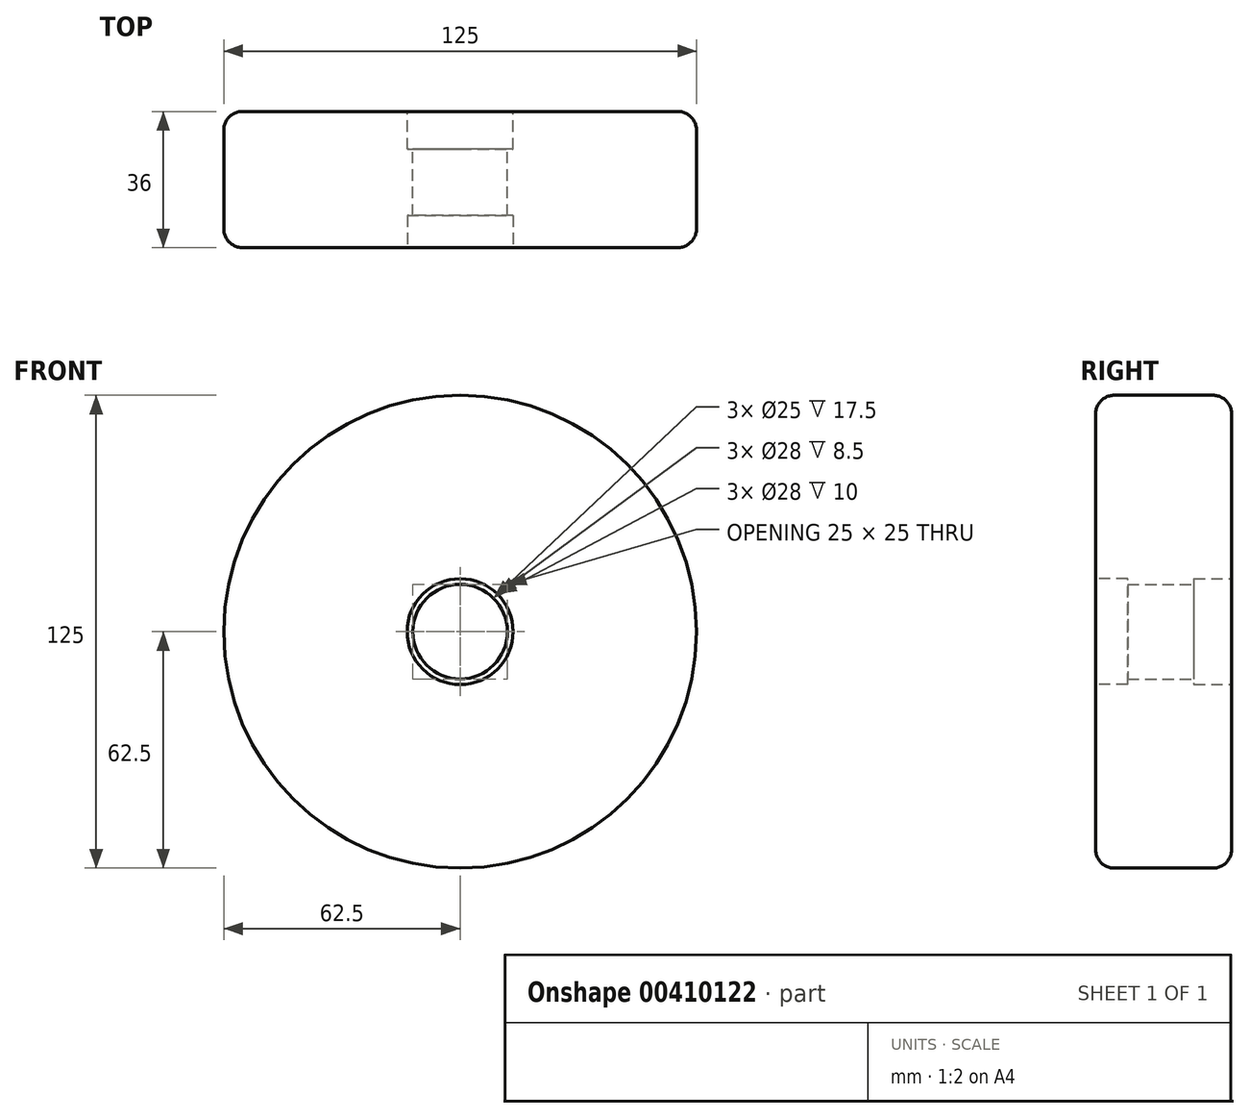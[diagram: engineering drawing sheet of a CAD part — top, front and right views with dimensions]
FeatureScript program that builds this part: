
annotation { "Feature Type Name" : "Feature", "Feature Type Description" : "" }
export const myFeature = defineFeature(function(context is Context, id is Id, definition is map)
    precondition{}
    {
        {
            var Q0;
            Q0=qCreatedBy(makeId("Front.planeOp"),FACE);
            var sketch = newSketch(context, id + "F0", { "sketchPlane" : qUnion([Q0])});
            skCircle(sketch, "E0", {"center": v(0, 0) * mm, "radius": 62.5 * mm});
            skSolve(sketch);
        }
        {
            var Q0;
            Q0=qSketchRegion(id+"F0",true);
            extrude(context, id + "F1", {"entities" : qUnion([Q0]), "depth" : 36 * mm});
        }
        {
            var Q0;
            Q0=makeQuery(id+"F1.opExtrude","CAP_EDGE",EDGE,{"disambiguationData":[OSD([sQuery(id+"F0.wireOp",EDGE,"E0")])],"isStart":false});
            var Q1;
            Q1=makeQuery(id+"F1.opExtrude","CAP_EDGE",EDGE,{"disambiguationData":[OSD([sQuery(id+"F0.wireOp",EDGE,"E0")])],"isStart":true});
            fillet(context, id + "F2", {"entities" : qUnion([Q0, Q1]), "radius" : 5 * mm, "tangentPropagation" : true, "allowEdgeOverflow" : false});
        }
        {
            var Q0;
            Q0=makeQuery(id+"F1.opExtrude","CAP_FACE",FACE,{"disambiguationData":[OSD([sQuery(id+"F0.wireOp",EDGE,"E0")])],"isStart":true});
            var sketch = newSketch(context, id + "F3", { "sketchPlane" : qUnion([Q0])});
            skCircle(sketch, "E1", {"center": v(0, 0) * mm, "radius": 12.5 * mm});
            skSolve(sketch);
        }
        {
            var Q0;
            Q0=makeQuery(id+"F3.imprint","IMPRINT",FACE,{"disambiguationData":[TD([[makeQuery(id+"F3.imprint","IMPRINT",EDGE,{"derivedFrom":sQuery(id+"F3.wireOp",EDGE,"E1")}),1.0]])]});
            var Q1;
            Q1=makeQuery(id+"F1.opExtrude","CAP_FACE",FACE,{"disambiguationData":[OSD([sQuery(id+"F0.wireOp",EDGE,"E0")])],"isStart":false});
            extrude(context, id + "F4", {"entities" : qUnion([Q0]), "operationType" : NewBodyOperationType.REMOVE, "endBound" : BoundingType.THROUGH_ALL, "oppositeDirection" : true, "endBoundEntityFace" : qUnion([Q1]), "depth" : 25 * mm});
        }
        {
            var Q0;
            Q0=makeQuery(id+"F1.opExtrude","CAP_FACE",FACE,{"disambiguationData":[OSD([sQuery(id+"F0.wireOp",EDGE,"E0")])],"isStart":false});
            var sketch = newSketch(context, id + "F5", { "sketchPlane" : qUnion([Q0])});
            skCircle(sketch, "E2", {"center": v(0, 0) * mm, "radius": 14 * mm});
            skSolve(sketch);
        }
        {
            var Q0;
            Q0=qSketchRegion(id+"F5",true);
            var Q1;
            Q1=sQuery(id+"F5.wireOp",EDGE,"E2");
            extrude(context, id + "F6", {"entities" : qUnion([Q0]), "operationType" : NewBodyOperationType.REMOVE, "surfaceEntities" : qUnion([Q1]), "oppositeDirection" : true, "depth" : 8.5 * mm});
        }
        {
            var Q0;
            Q0=makeQuery(id+"F1.opExtrude","CAP_FACE",FACE,{"disambiguationData":[OSD([sQuery(id+"F0.wireOp",EDGE,"E0")])],"isStart":true});
            var sketch = newSketch(context, id + "F7", { "sketchPlane" : qUnion([Q0])});
            skCircle(sketch, "E3", {"center": v(0, 0) * mm, "radius": 14 * mm});
            skSolve(sketch);
        }
        {
            var Q0;
            Q0 = qSketchRegion(id + "F7", true);
            extrude(context, id + "F8", {"entities" : qUnion([Q0]), "operationType" : NewBodyOperationType.REMOVE, "oppositeDirection" : true, "depth" : 10 * mm});
        }
    });
